# Revit family: Haworth_BuzziPicNic_Bench
name_source: partatom
category: Furniture
revit_build: Autodesk Revit 2018 (Build: 20170223_1515(x64)
units: mm (PartAtom-declared; Revit-internal decimal feet)

## family parameters
Always vertical = Yes
Cut with Voids When Loaded = No
OmniClass Number = 23.40.20.00
OmniClass Title = General Furniture and Specialties
Room Calculation Point = No
Shared = No
Work Plane-Based = No

## types (2) — shared parameters
Actual Depth = 17 205/256"
Actual Height = 17 77/128"
Assembly Code = E2020200
Cushion = Yes
Glide Finish = Haworth _ Polymer _ Black
Manufacturer = Haworth
Model = HCBZ-PNB
Note = Verify Final Dim. w/ Haworth
Revision = 1
URL = http://www.haworth.com
URL - Product = https://www.haworth.com
Warranty = http://www.haworth.com

## per-type parameters (varying)
| type | Actual Width | Description | Large | Small |
| HCBZ-PNB1-W | 45 169/256" | Haworth BuzziPicNic - Small Bench | No | Yes |
| HCBZ-PNB2-W | 53 69/128" | Haworth BuzziPicNic - Large Bench | Yes | No |

## geometry (parser evidence)
native form markers: Blend x15, Sweep x2
no freeform markers — native parametric forms only
